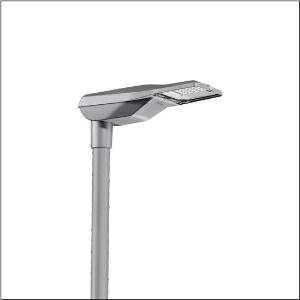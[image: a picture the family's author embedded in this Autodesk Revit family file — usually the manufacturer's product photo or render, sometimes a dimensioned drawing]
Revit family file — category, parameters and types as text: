
# Revit family: streetlight_sl_21_iq_micro___st0_8a_5xe1c61g08cb_671e
name_source: partatom
category: Lighting Fixtures
units: mm (PartAtom-declared; Revit-internal decimal feet)

## family parameters
Cut with Voids When Loaded = No
Host = Face
Light Source = No
Part Type = Normal
Room Calculation Point = No
Round Connector Dimension = Use Diameter
Shared = No

## types (1)
- --- (1 x LED, 2570 lm, 19.4 W, 2700K)
    Apparent Load = 19 VA
    CIE Flux Codes = 38 75 97 100 100
    Color Rendering = 70
    Color Temperature = 2700K
    Default Elevation = 1800 mm
    Description = Streetlight SL 21 iQ micro, mast luminaire, primary light control with lens, of PMMA, primary optical cover: cover, of toughened safety glass, transparent, light distribution: ST0.8a, light emission: direct distribution, primary light characteristic: asymmetric, installation type: post-top, side-entry, LED, High Power LED, rated luminous flux: 2.570lm, luminous efficacy: 133lm/W, light colour: 727, colour temperature: 2700K, control: Street-Remote, Auto-Match, Temp-Guard, Lumen-Switch, Night-Set, Smart-Wire, Light-Fading, Desk-Remote (wireless, voltage-free reading and setting of iQ features in the workshop via application-optimized NFC function/RFID function), optimised constant luminous flux control (CLO 2.0), presetting dimming linear, mains connection: 220..240V, AC, 50/60Hz, start of lifetime: 19W, end of service life: 20W, reduction: 10W, luminaire housing, of diecast aluminium, powder-coated, Siteco® metallic grey (DB 702S), corrosivity category C5 mid according to DIN EN ISO 12944, please order mast flange separately, inclination adjustable: 0°, 5°, 10°, 15°, sealing non-destructively replaceable, multi-level sealing system, length: 528mm, width: 235mm, height: 110mm, mast flange for spigot size: 42mm (side-entry): 5XC10008XM4, 60/48mm (side-entry/post-top): 5XC10108XM2, 76/60mm (side-entry/post-top): 5XC10108XM1, protection rating (complete): IP66, insulation class (complete): insulation class II (safety insulation), certification: CE, ENEC, ENEC+, VDE, impact resistance: IK09, permissible operating ambient temperature for outdoor applications: -40..+50°C, standard-compliant lighting for roads and squares, packaging unit: 1 piece

Light Distribution: ST0.8a
    Height = 110 mm
    Lamp = 1 x LED
    Lamp Light Flux = 2570 lm
    Lamp Power = 19.4 W
    Lamp count = 1
    Length = 528 mm
    Luminous efficacy = 132 lm/W
    Manufacturer = Siteco
    ModVariant = No
    Model = 5XE1C61G08CB
    Number of Poles = 1
    OnlyDefault = Yes
    Power Factor = 1
    Product Name = Streetlight SL 21 iQ micro | ST0.8a
    Product group = mast luminaire | pylon top
    ProductGroupID = 6100
    Protection Class = Protection class II
    Protection Degree = IP 66
    RLX_Detail_Level = 1
    RLX_Emergency_Light_Flux = 0 lm
    RLX_Emergency_Type = 0
    RLX_Emergency_Type_DB = No
    RlxData = <blob elided: 99929 chars, md5=74c222fe>
    Socket = socket
    Standby Power = 0 W
    System Light Flux = 2570 lm
    System Power = 19 W
    Type Comments = factory setting: luminous flux: 100 % | dim-lin: 254 | 387 mA
    Type Image = l_1006881.jpg
    URL = http://relux.com
    VarID = @adj_069609
    Voltage = 0 V
    Weight = 0.00 kg
    Width = 235 mm

## geometry (parser evidence)
native form markers: Blend x4, Sweep x10
no freeform markers — native parametric forms only
